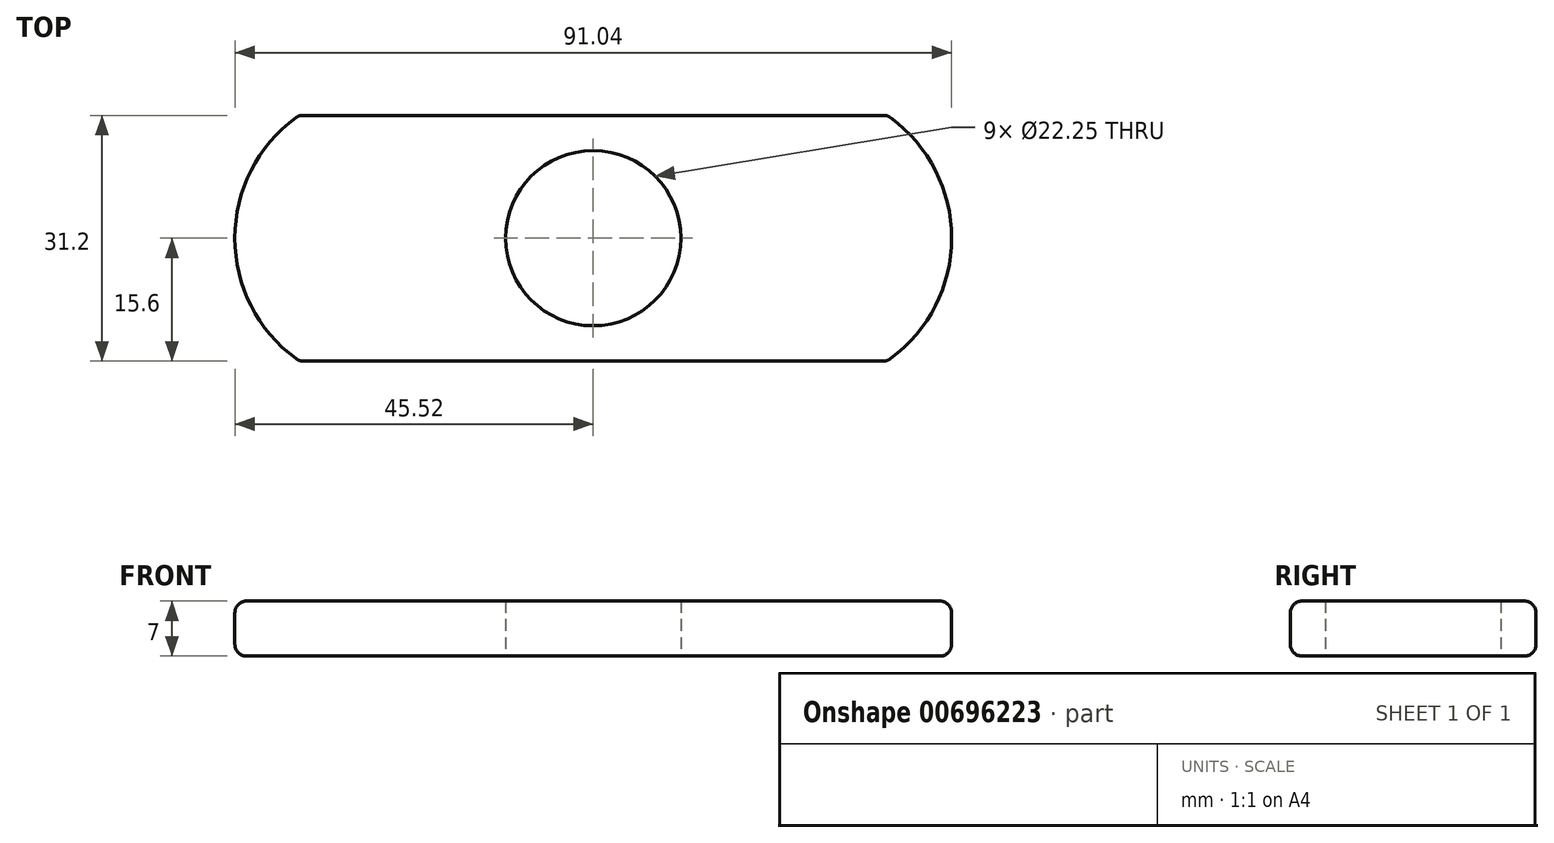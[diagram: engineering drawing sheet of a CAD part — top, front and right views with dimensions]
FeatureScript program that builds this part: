
annotation { "Feature Type Name" : "Feature", "Feature Type Description" : "" }
export const myFeature = defineFeature(function(context is Context, id is Id, definition is map)
    precondition{}
    {
        {
            var Q0;
            Q0=qCreatedBy(makeId("Top.planeOp"),FACE);
            var sketch = newSketch(context, id + "F0", { "sketchPlane" : qUnion([Q0])});
            skCircle(sketch, "E0", {"center": v(0, 0) * mm, "radius": 11.12 * mm});
            skLineSegment(sketch, "E1", {"start": v(-37.36, 15.6) * mm, "end": v(38.63, 15.6) * mm});
            skLineSegment(sketch, "E2.MirrorCS", {"start": v(-37.36, -15.6) * mm, "end": v(38.63, -15.6) * mm});
            skArc(sketch, "E3", {"start": v(-37.36, 15.6) * mm, "mid": v(-45.52, 0) * mm, "end": v(-37.36, -15.6) * mm});
            skArc(sketch, "E4.MirrorCS", {"start": v(37.36, 15.6) * mm, "mid": v(45.52, 0) * mm, "end": v(37.36, -15.6) * mm});
            skSolve(sketch);
        }
        {
            var Q0;
            Q0=makeQuery(id+"F0.imprint","IMPRINT",FACE,{"disambiguationData":[TD([[makeQuery(id+"F0.imprint","IMPRINT",EDGE,{"derivedFrom":sQuery(id+"F0.wireOp",EDGE,"E0")}),-1.0]])]});
            extrude(context, id + "F1", {"entities" : qUnion([Q0]), "depth" : 7 * mm, "offsetDistance" : 25 * mm});
        }
        {
            var Q0;
            Q0=makeQuery(id+"F1.opExtrude","CAP_EDGE",EDGE,{"disambiguationData":[OSD([sQuery(id+"F0.wireOp",EDGE,"E2.MirrorCS")])],"isStart":false});
            var Q1;
            Q1=makeQuery(id+"F1.opExtrude","CAP_EDGE",EDGE,{"disambiguationData":[OSD([sQuery(id+"F0.wireOp",EDGE,"E2.MirrorCS")])],"isStart":true});
            var Q2;
            Q2=makeQuery(id+"F1.opExtrude","CAP_EDGE",EDGE,{"disambiguationData":[OSD([sQuery(id+"F0.wireOp",EDGE,"E3")])],"isStart":false});
            var Q3;
            Q3=makeQuery(id+"F1.opExtrude","CAP_EDGE",EDGE,{"disambiguationData":[OSD([sQuery(id+"F0.wireOp",EDGE,"E3")])],"isStart":true});
            var Q4;
            Q4=makeQuery(id+"F1.opExtrude","CAP_EDGE",EDGE,{"disambiguationData":[OSD([sQuery(id+"F0.wireOp",EDGE,"E1")])],"isStart":false});
            var Q5;
            Q5=makeQuery(id+"F1.opExtrude","CAP_EDGE",EDGE,{"disambiguationData":[OSD([sQuery(id+"F0.wireOp",EDGE,"E1")])],"isStart":true});
            var Q6;
            Q6=makeQuery(id+"F1.opExtrude","CAP_EDGE",EDGE,{"disambiguationData":[OSD([sQuery(id+"F0.wireOp",EDGE,"E4.MirrorCS")])],"isStart":false});
            var Q7;
            Q7=makeQuery(id+"F1.opExtrude","CAP_EDGE",EDGE,{"disambiguationData":[OSD([sQuery(id+"F0.wireOp",EDGE,"E4.MirrorCS")])],"isStart":true});
            var Q8;
            Q8=makeQuery(id+"F1.opExtrude","SWEPT_EDGE",EDGE,{"disambiguationData":[OSD([sQuery(id+"F0.wireOp",EDGE,"E1"),sQuery(id+"F0.wireOp",EDGE,"E4.MirrorCS")])]});
            var Q9;
            Q9=makeQuery(id+"F1.opExtrude","SWEPT_EDGE",EDGE,{"disambiguationData":[OSD([sQuery(id+"F0.wireOp",EDGE,"E1"),sQuery(id+"F0.wireOp",EDGE,"E3")])]});
            var Q10;
            Q10=makeQuery(id+"F1.opExtrude","SWEPT_EDGE",EDGE,{"disambiguationData":[OSD([sQuery(id+"F0.wireOp",EDGE,"E2.MirrorCS"),sQuery(id+"F0.wireOp",EDGE,"E3")])]});
            var Q11;
            Q11=makeQuery(id+"F1.opExtrude","SWEPT_EDGE",EDGE,{"disambiguationData":[OSD([sQuery(id+"F0.wireOp",EDGE,"E2.MirrorCS"),sQuery(id+"F0.wireOp",EDGE,"E4.MirrorCS")])]});
            fillet(context, id + "F2", {"entities" : qUnion([Q0, Q1, Q2, Q3, Q4, Q5, Q6, Q7, Q8, Q9, Q10, Q11]), "radius" : 1.5 * mm, "tangentPropagation" : true, "allowEdgeOverflow" : false});
        }
    });
